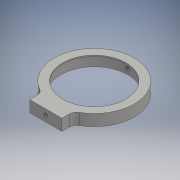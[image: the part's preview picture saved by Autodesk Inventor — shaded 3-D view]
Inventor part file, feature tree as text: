
AUTODESK INVENTOR PART (.ipt)
format: ipt  version: 2016 (Build 200138000, 138)  size: 177,152 bytes
history: native  units: mm
features: fillet x6, sketch x5, extrude x3, hole x2, plane x1
ambient origin geometry x8: Origin, YZ Plane, XZ Plane, XY Plane, X Axis, Y Axis, Z Axis, Center Point
bodies: Solid1 (feature_tree)
feature tree (17):
  extrude  "Extrusion1"  Depth=6.0mm
  fillet  "Fillet1"  Radius=62.8mm
  fillet  "Fillet2"  Radius=8.726646mm
  fillet  "Fillet3"  Radius=8.0mm
  fillet  "Fillet4"  Radius=6.0mm
  extrude  "Extrusion2"  Depth=6.0mm
  plane  "Work Plane1"
  hole  "Hole1"  [1 undecoded]
  extrude  "Extrusion3"  Depth=4.0mm
  fillet  "Fillet5"  Radius=38.1mm
  fillet  "Fillet6"  Radius=25.4mm
  hole  "Hole2"  [1 undecoded]
  sketch  "Sketch1"  dims[d0=50.8mm d1=52.8mm d2=62.8mm d4=8.726646mm d5=8.0mm d6=0.0mm d7=6.0mm]
  sketch  "Sketch2"  dims[d8=6.0mm d9=6.0mm]
  sketch  "Sketch3"  dims[d10=6.0mm d11=49.8mm]
  sketch  "Sketch4"  dims[d12=1.0mm d13=0.0mm d14=4.0mm]
  sketch  "Sketch5"  dims[d15=3.302mm d16=8.331mm d17=4.0mm d18=2.0mm d19=90.0deg d20=12.3mm d21=20.594885mm d22=38.1mm d23=25.4mm d24=9.0mm d25=0.0mm d26=6.0mm d27=6.0mm d28=3.242mm d29=8.0mm d30=4.0mm d31=2.0mm d32=90.0deg d33=13.0mm d34=20.594885mm]
note: 2 required parameter values undecoded (feature->parameter linkage not recoverable at this tier; creation-order binding heuristic only, values carry confidence <= 0.55)
